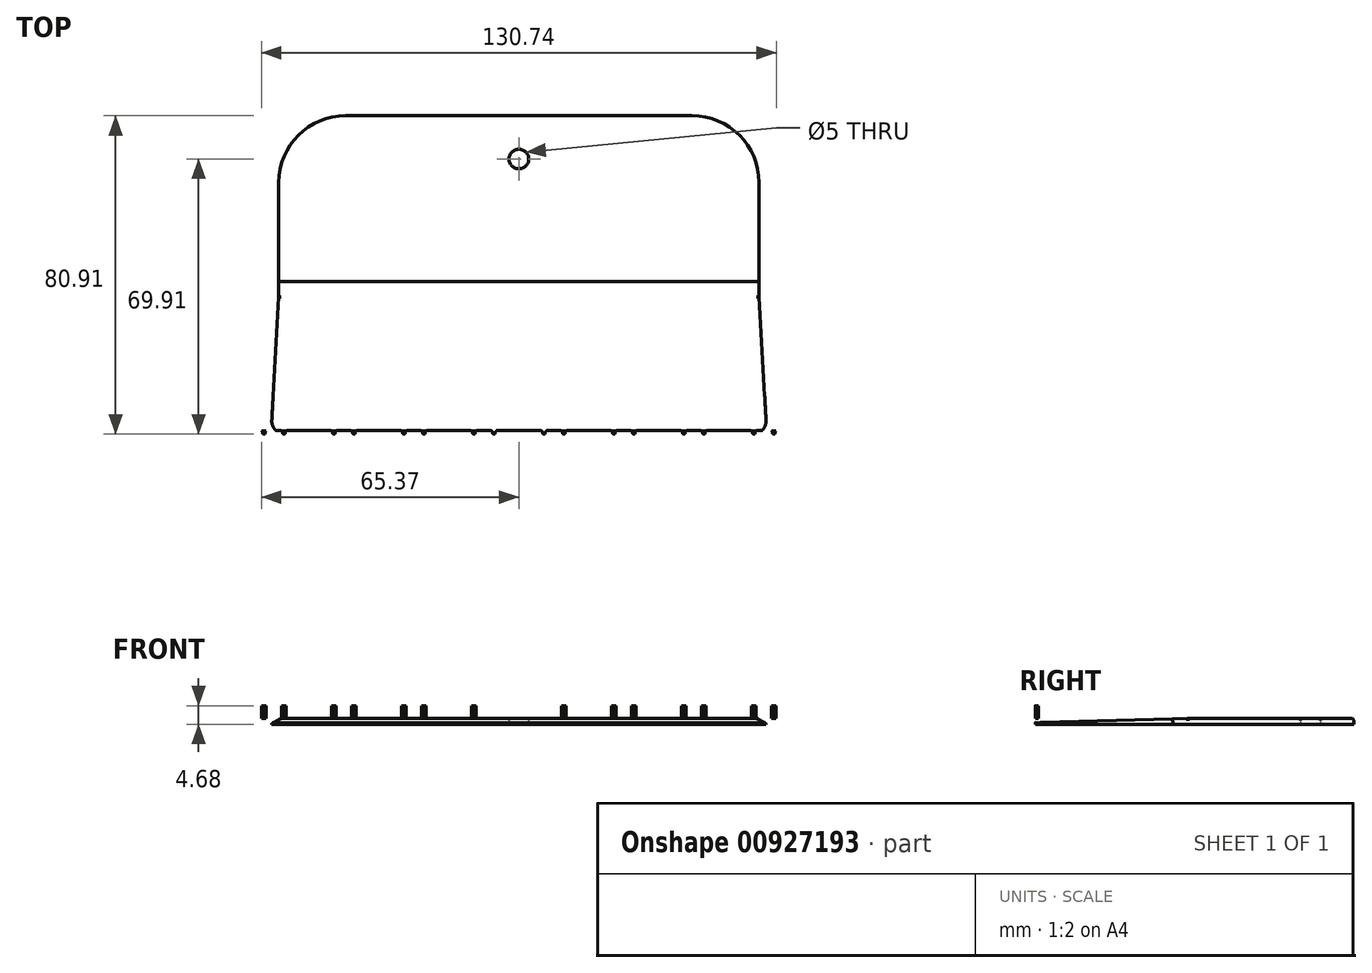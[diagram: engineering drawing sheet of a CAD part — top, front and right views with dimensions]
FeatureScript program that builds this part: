
annotation { "Feature Type Name" : "Feature", "Feature Type Description" : "" }
export const myFeature = defineFeature(function(context is Context, id is Id, definition is map)
    precondition{}
    {
        {
            var Q0;
            Q0=qCreatedBy(makeId("Top.planeOp"),FACE);
            var sketch = newSketch(context, id + "F0", { "sketchPlane" : qUnion([Q0])});
            skLineSegment(sketch, "E0.top", {"start": v(44, 40.5) * mm, "end": v(-44, 40.5) * mm});
            skPoint(sketch, "E1.orphan", {"position": v(61, 42) * mm});
            skPoint(sketch, "E2.orphan", {"position": v(-61, 42) * mm});
            skLineSegment(sketch, "E3", {"start": v(-74.02, -5.5) * mm, "end": v(79.96, -5.5) * mm, "construction": true});
            skPoint(sketch, "E4.orphan", {"position": v(-63, 40.5) * mm});
            skPoint(sketch, "E5.orphan", {"position": v(63, 40.5) * mm});
            skLineSegment(sketch, "E6.trimOffspring", {"start": v(-61, -5.5) * mm, "end": v(-61, 23.5) * mm});
            skLineSegment(sketch, "E7.trimOffspring", {"start": v(61, -5.5) * mm, "end": v(61, 23.5) * mm});
            skLineSegment(sketch, "E8", {"start": v(-61, -5.5) * mm, "end": v(-62.79, -36.8) * mm});
            skLineSegment(sketch, "E9", {"start": v(61, -5.5) * mm, "end": v(62.79, -36.8) * mm});
            skArc(sketch, "E10.filletArc", {"start": v(59.3, -40.5) * mm, "mid": v(61.84, -39.4) * mm, "end": v(62.79, -36.8) * mm});
            skArc(sketch, "E11.filletArc", {"start": v(-62.79, -36.8) * mm, "mid": v(-61.84, -39.4) * mm, "end": v(-59.3, -40.5) * mm});
            skPoint(sketch, "E12.visualSharp", {"position": v(-61, 40.5) * mm});
            skArc(sketch, "E12.filletArc", {"start": v(-44, 40.5) * mm, "mid": v(-56.02, 35.52) * mm, "end": v(-61, 23.5) * mm});
            skPoint(sketch, "E13.visualSharp", {"position": v(61, 40.5) * mm});
            skArc(sketch, "E13.filletArc", {"start": v(61, 23.5) * mm, "mid": v(56.02, 35.52) * mm, "end": v(44, 40.5) * mm});
            skCircle(sketch, "E14", {"center": v(0, 29.5) * mm, "radius": 2.5 * mm});
            skLineSegment(sketch, "E15", {"start": v(-59.3, -40.5) * mm, "end": v(59.3, -40.5) * mm});
            skPoint(sketch, "E15.endSnap0", {"position": v(59.3, -40.5) * mm});
            skSolve(sketch);
        }
        {
            var Q0;
            Q0 = qSketchRegion(id + "F0", true);
            extrude(context, id + "F1", {"entities" : qUnion([Q0]), "depth" : 1.5 * mm, "offsetDistance" : 25 * mm});
        }
        {
            var Q0;
            Q0=makeQuery(id+"F1.opExtrude","CAP_FACE",FACE,{"disambiguationData":[OSD([sQuery(id+"F0.wireOp",EDGE,"E0.top"),sQuery(id+"F0.wireOp",EDGE,"E6.trimOffspring"),sQuery(id+"F0.wireOp",EDGE,"E7.trimOffspring"),sQuery(id+"F0.wireOp",EDGE,"E8"),sQuery(id+"F0.wireOp",EDGE,"E9"),sQuery(id+"F0.wireOp",EDGE,"E10.filletArc"),sQuery(id+"F0.wireOp",EDGE,"E11.filletArc"),sQuery(id+"F0.wireOp",EDGE,"E12.filletArc"),sQuery(id+"F0.wireOp",EDGE,"E13.filletArc"),sQuery(id+"F0.wireOp",EDGE,"E14"),sQuery(id+"F0.wireOp",EDGE,"E15")])],"isStart":false});
            var sketch = newSketch(context, id + "F2", { "sketchPlane" : qUnion([Q0])});
            skLineSegment(sketch, "E16.3.0.1", {"start": v(-45.36, -39.59) * mm, "end": v(-56.24, -39.59) * mm});
            skPoint(sketch, "E16.4.0.0", {"position": v(-57.15, -39.97) * mm});
            skArc(sketch, "E16.4.0.3", {"start": v(-57.45, -40.2) * mm, "mid": v(-57.15, -40.5) * mm, "end": v(-56.85, -40.2) * mm});
            skLineSegment(sketch, "E16.4.0.5", {"start": v(-57.15, -39.2) * mm, "end": v(-57.15, -39.9) * mm, "construction": true});
            skArc(sketch, "E17.filletArc", {"start": v(-56.24, -39.59) * mm, "mid": v(-56.67, -39.76) * mm, "end": v(-56.85, -40.2) * mm});
            skPoint(sketch, "E18.visualSharp", {"position": v(-57.45, -39.2) * mm});
            skArc(sketch, "E19.MirrorCS", {"start": v(-58.06, -39.59) * mm, "mid": v(-57.63, -39.76) * mm, "end": v(-57.45, -40.2) * mm});
            skLineSegment(sketch, "E20.MirrorCS", {"start": v(-69.35, -39.59) * mm, "end": v(-58.06, -39.59) * mm});
            skArc(sketch, "E21.1.0.0", {"start": v(-45.36, -39.59) * mm, "mid": v(-44.93, -39.76) * mm, "end": v(-44.75, -40.2) * mm});
            skArc(sketch, "E21.1.0.1", {"start": v(-44.75, -40.2) * mm, "mid": v(-44.45, -40.5) * mm, "end": v(-44.15, -40.2) * mm});
            skArc(sketch, "E21.1.0.2", {"start": v(-43.54, -39.59) * mm, "mid": v(-43.97, -39.76) * mm, "end": v(-44.15, -40.2) * mm});
            skLineSegment(sketch, "E21.1.0.3", {"start": v(-32.66, -39.59) * mm, "end": v(-43.54, -39.59) * mm});
            skArc(sketch, "E21.2.0.0", {"start": v(-32.66, -39.59) * mm, "mid": v(-32.23, -39.76) * mm, "end": v(-32.05, -40.2) * mm});
            skArc(sketch, "E21.2.0.1", {"start": v(-32.05, -40.2) * mm, "mid": v(-31.75, -40.5) * mm, "end": v(-31.45, -40.2) * mm});
            skArc(sketch, "E21.2.0.2", {"start": v(-30.84, -39.59) * mm, "mid": v(-31.27, -39.76) * mm, "end": v(-31.45, -40.2) * mm});
            skLineSegment(sketch, "E21.2.0.3", {"start": v(-19.96, -39.59) * mm, "end": v(-30.84, -39.59) * mm});
            skArc(sketch, "E21.3.0.0", {"start": v(-19.96, -39.59) * mm, "mid": v(-19.53, -39.76) * mm, "end": v(-19.35, -40.2) * mm});
            skArc(sketch, "E21.3.0.1", {"start": v(-19.35, -40.2) * mm, "mid": v(-19.05, -40.5) * mm, "end": v(-18.75, -40.2) * mm});
            skArc(sketch, "E21.3.0.2", {"start": v(-18.14, -39.59) * mm, "mid": v(-18.57, -39.76) * mm, "end": v(-18.75, -40.2) * mm});
            skLineSegment(sketch, "E21.3.0.3", {"start": v(-6.85, -39.59) * mm, "end": v(-18.14, -39.59) * mm});
            skArc(sketch, "E21.4.0.0", {"start": v(-7.26, -39.59) * mm, "mid": v(-6.83, -39.76) * mm, "end": v(-6.65, -40.2) * mm});
            skArc(sketch, "E21.4.0.1", {"start": v(-6.65, -40.2) * mm, "mid": v(-6.35, -40.5) * mm, "end": v(-6.05, -40.2) * mm});
            skArc(sketch, "E21.4.0.2", {"start": v(-5.44, -39.59) * mm, "mid": v(-5.87, -39.76) * mm, "end": v(-6.05, -40.2) * mm});
            skLineSegment(sketch, "E21.4.0.3", {"start": v(5.85, -39.59) * mm, "end": v(-5.44, -39.59) * mm});
            skArc(sketch, "E21.5.0.0", {"start": v(5.44, -39.59) * mm, "mid": v(5.87, -39.76) * mm, "end": v(6.05, -40.2) * mm});
            skArc(sketch, "E21.5.0.1", {"start": v(6.05, -40.2) * mm, "mid": v(6.35, -40.5) * mm, "end": v(6.65, -40.2) * mm});
            skArc(sketch, "E21.5.0.2", {"start": v(7.26, -39.59) * mm, "mid": v(6.83, -39.76) * mm, "end": v(6.65, -40.2) * mm});
            skLineSegment(sketch, "E21.5.0.3", {"start": v(18.55, -39.59) * mm, "end": v(7.26, -39.59) * mm});
            skArc(sketch, "E21.6.0.0", {"start": v(18.14, -39.59) * mm, "mid": v(18.57, -39.76) * mm, "end": v(18.75, -40.2) * mm});
            skArc(sketch, "E21.6.0.1", {"start": v(18.75, -40.2) * mm, "mid": v(19.05, -40.5) * mm, "end": v(19.35, -40.2) * mm});
            skArc(sketch, "E21.6.0.2", {"start": v(19.96, -39.59) * mm, "mid": v(19.53, -39.76) * mm, "end": v(19.35, -40.2) * mm});
            skLineSegment(sketch, "E21.6.0.3", {"start": v(31.25, -39.59) * mm, "end": v(19.96, -39.59) * mm});
            skArc(sketch, "E21.7.0.0", {"start": v(30.84, -39.59) * mm, "mid": v(31.27, -39.76) * mm, "end": v(31.45, -40.2) * mm});
            skArc(sketch, "E21.7.0.1", {"start": v(31.45, -40.2) * mm, "mid": v(31.75, -40.5) * mm, "end": v(32.05, -40.2) * mm});
            skArc(sketch, "E21.7.0.2", {"start": v(32.66, -39.59) * mm, "mid": v(32.23, -39.76) * mm, "end": v(32.05, -40.2) * mm});
            skLineSegment(sketch, "E21.7.0.3", {"start": v(43.95, -39.59) * mm, "end": v(32.66, -39.59) * mm});
            skArc(sketch, "E21.8.0.0", {"start": v(43.54, -39.59) * mm, "mid": v(43.97, -39.76) * mm, "end": v(44.15, -40.2) * mm});
            skArc(sketch, "E21.8.0.1", {"start": v(44.15, -40.2) * mm, "mid": v(44.45, -40.5) * mm, "end": v(44.75, -40.2) * mm});
            skArc(sketch, "E21.8.0.2", {"start": v(45.36, -39.59) * mm, "mid": v(44.93, -39.76) * mm, "end": v(44.75, -40.2) * mm});
            skLineSegment(sketch, "E21.8.0.3", {"start": v(56.65, -39.59) * mm, "end": v(45.36, -39.59) * mm});
            skArc(sketch, "E21.9.0.0", {"start": v(56.24, -39.59) * mm, "mid": v(56.67, -39.76) * mm, "end": v(56.85, -40.2) * mm});
            skArc(sketch, "E21.9.0.1", {"start": v(56.85, -40.2) * mm, "mid": v(57.15, -40.5) * mm, "end": v(57.45, -40.2) * mm});
            skArc(sketch, "E21.9.0.2", {"start": v(58.06, -39.59) * mm, "mid": v(57.63, -39.76) * mm, "end": v(57.45, -40.2) * mm});
            skLineSegment(sketch, "E21.9.0.3", {"start": v(69.35, -39.59) * mm, "end": v(58.06, -39.59) * mm});
            skLineSegment(sketch, "E21.direction1", {"start": v(-58.06, -40.2) * mm, "end": v(-45.36, -40.2) * mm, "construction": true});
            skPoint(sketch, "E22.orphan", {"position": v(-44.95, -39.59) * mm});
            skPoint(sketch, "E23.orphan", {"position": v(-32.25, -39.59) * mm});
            skPoint(sketch, "E24.orphan", {"position": v(-19.55, -39.59) * mm});
            skLineSegment(sketch, "E25", {"start": v(-69.35, -39.59) * mm, "end": v(-69.35, -63.5) * mm});
            skLineSegment(sketch, "E26", {"start": v(-69.35, -63.5) * mm, "end": v(69.35, -63.5) * mm});
            skLineSegment(sketch, "E27", {"start": v(69.35, -63.5) * mm, "end": v(69.35, -39.59) * mm});
            skSolve(sketch);
        }
        {
            var Q0;
            Q0=qCreatedBy(makeId("Right.planeOp"),FACE);
            var sketch = newSketch(context, id + "F3", { "sketchPlane" : qUnion([Q0])});
            skLineSegment(sketch, "E28", {"start": v(0, 1.55) * mm, "end": v(-43.24, 0.26) * mm});
            skLineSegment(sketch, "E29", {"start": v(-43.24, 0.26) * mm, "end": v(-43.4, 5.8) * mm});
            skLineSegment(sketch, "E30", {"start": v(-43.4, 5.8) * mm, "end": v(0, 5.8) * mm});
            skLineSegment(sketch, "E31", {"start": v(0, 5.8) * mm, "end": v(0, 1.55) * mm});
            skSolve(sketch);
        }
        {
            var Q0;
            Q0 = qSketchRegion(id + "F3", true);
            extrude(context, id + "F4", {"entities" : qUnion([Q0]), "operationType" : NewBodyOperationType.REMOVE, "endBound" : BoundingType.SYMMETRIC, "oppositeDirection" : true, "depth" : 152.4 * mm, "offsetDistance" : 25.4 * mm});
        }
        {
            var Q0;
            Q0=makeQuery(id+"F1.opExtrude","CAP_EDGE",EDGE,{"disambiguationData":[OSD([sQuery(id+"F0.wireOp",EDGE,"E0.top")])],"isStart":false});
            fillet(context, id + "F5", {"entities" : qUnion([Q0]), "radius" : 0.64 * mm, "tangentPropagation" : true, "allowEdgeOverflow" : false});
        }
        {
            var Q0;
            Q0=makeQuery(id+"F1.opExtrude","CAP_EDGE",EDGE,{"disambiguationData":[OSD([sQuery(id+"F0.wireOp",EDGE,"E14")])],"isStart":false});
            fillet(context, id + "F6", {"entities" : qUnion([Q0]), "radius" : 0.5 * mm, "tangentPropagation" : true, "allowEdgeOverflow" : false});
        }
        {
            var Q0;
            Q0 = qSketchRegion(id + "F2", true);
            extrude(context, id + "F7", {"entities" : qUnion([Q0]), "depth" : 3.17 * mm, "offsetDistance" : 25.4 * mm});
        }
        {
            var Q0;
            Q0=qCreatedBy(makeId("Top.planeOp"),FACE);
            var sketch = newSketch(context, id + "F8", { "sketchPlane" : qUnion([Q0])});
            skArc(sketch, "E32", {"start": v(6.05, -40.11) * mm, "mid": v(6.35, -40.41) * mm, "end": v(6.65, -40.11) * mm});
            skArc(sketch, "E33", {"start": v(6.05, -40.11) * mm, "mid": v(5.87, -39.68) * mm, "end": v(5.44, -39.5) * mm});
            skLineSegment(sketch, "E34", {"start": v(-5.44, -39.5) * mm, "end": v(5.44, -39.5) * mm});
            skArc(sketch, "E35", {"start": v(-5.44, -39.5) * mm, "mid": v(-5.87, -39.68) * mm, "end": v(-6.05, -40.11) * mm});
            skArc(sketch, "E36", {"start": v(-6.65, -40.11) * mm, "mid": v(-6.35, -40.41) * mm, "end": v(-6.05, -40.11) * mm});
            skArc(sketch, "E37", {"start": v(-6.65, -40.11) * mm, "mid": v(-6.83, -39.68) * mm, "end": v(-7.26, -39.5) * mm});
            skLineSegment(sketch, "E38", {"start": v(-8.89, -39.5) * mm, "end": v(-7.26, -39.5) * mm});
            skLineSegment(sketch, "E39", {"start": v(7.26, -39.5) * mm, "end": v(8.89, -39.5) * mm});
            skArc(sketch, "E40", {"start": v(7.26, -39.5) * mm, "mid": v(6.83, -39.68) * mm, "end": v(6.65, -40.11) * mm});
            skArc(sketch, "E41", {"start": v(23.83, -40.11) * mm, "mid": v(24.13, -40.41) * mm, "end": v(24.43, -40.11) * mm});
            skArc(sketch, "E42", {"start": v(23.83, -40.11) * mm, "mid": v(23.65, -39.68) * mm, "end": v(23.22, -39.5) * mm});
            skLineSegment(sketch, "E43", {"start": v(12.34, -39.5) * mm, "end": v(23.22, -39.5) * mm});
            skArc(sketch, "E44", {"start": v(12.34, -39.5) * mm, "mid": v(11.9, -39.68) * mm, "end": v(11.73, -40.11) * mm});
            skArc(sketch, "E45", {"start": v(11.13, -40.11) * mm, "mid": v(11.43, -40.41) * mm, "end": v(11.73, -40.11) * mm});
            skArc(sketch, "E46", {"start": v(11.13, -40.11) * mm, "mid": v(10.95, -39.68) * mm, "end": v(10.52, -39.5) * mm});
            skLineSegment(sketch, "E47", {"start": v(8.89, -39.5) * mm, "end": v(10.52, -39.5) * mm});
            skLineSegment(sketch, "E48", {"start": v(25.04, -39.5) * mm, "end": v(26.67, -39.5) * mm});
            skArc(sketch, "E49", {"start": v(25.04, -39.5) * mm, "mid": v(24.6, -39.68) * mm, "end": v(24.43, -40.11) * mm});
            skArc(sketch, "E50", {"start": v(41.61, -40.11) * mm, "mid": v(41.9, -40.41) * mm, "end": v(42.2, -40.11) * mm});
            skArc(sketch, "E51", {"start": v(41.61, -40.11) * mm, "mid": v(41.43, -39.68) * mm, "end": v(41, -39.5) * mm});
            skLineSegment(sketch, "E52", {"start": v(30.12, -39.5) * mm, "end": v(41, -39.5) * mm});
            skArc(sketch, "E53", {"start": v(30.12, -39.5) * mm, "mid": v(29.69, -39.68) * mm, "end": v(29.5, -40.11) * mm});
            skArc(sketch, "E54", {"start": v(28.91, -40.11) * mm, "mid": v(29.2, -40.41) * mm, "end": v(29.5, -40.11) * mm});
            skArc(sketch, "E55", {"start": v(28.91, -40.11) * mm, "mid": v(28.73, -39.68) * mm, "end": v(28.3, -39.5) * mm});
            skLineSegment(sketch, "E56", {"start": v(26.67, -39.5) * mm, "end": v(28.3, -39.5) * mm});
            skLineSegment(sketch, "E57", {"start": v(42.82, -39.5) * mm, "end": v(44.45, -39.5) * mm});
            skArc(sketch, "E58", {"start": v(42.82, -39.5) * mm, "mid": v(42.39, -39.68) * mm, "end": v(42.2, -40.11) * mm});
            skArc(sketch, "E59", {"start": v(59.4, -40.11) * mm, "mid": v(59.69, -40.41) * mm, "end": v(59.99, -40.11) * mm});
            skArc(sketch, "E60", {"start": v(59.4, -40.11) * mm, "mid": v(59.21, -39.68) * mm, "end": v(58.78, -39.5) * mm});
            skLineSegment(sketch, "E61", {"start": v(47.9, -39.5) * mm, "end": v(58.78, -39.5) * mm});
            skArc(sketch, "E62", {"start": v(47.9, -39.5) * mm, "mid": v(47.47, -39.68) * mm, "end": v(47.29, -40.11) * mm});
            skArc(sketch, "E63", {"start": v(46.7, -40.11) * mm, "mid": v(46.99, -40.41) * mm, "end": v(47.29, -40.11) * mm});
            skArc(sketch, "E64", {"start": v(46.7, -40.11) * mm, "mid": v(46.51, -39.68) * mm, "end": v(46.08, -39.5) * mm});
            skLineSegment(sketch, "E65", {"start": v(44.45, -39.5) * mm, "end": v(46.08, -39.5) * mm});
            skLineSegment(sketch, "E66", {"start": v(60.6, -39.5) * mm, "end": v(62.23, -39.5) * mm});
            skArc(sketch, "E67", {"start": v(60.6, -39.5) * mm, "mid": v(60.17, -39.68) * mm, "end": v(59.99, -40.11) * mm});
            skArc(sketch, "E68", {"start": v(77.17, -40.11) * mm, "mid": v(77.47, -40.41) * mm, "end": v(77.77, -40.11) * mm});
            skArc(sketch, "E69", {"start": v(77.17, -40.11) * mm, "mid": v(77, -39.68) * mm, "end": v(76.56, -39.5) * mm});
            skLineSegment(sketch, "E70", {"start": v(65.68, -39.5) * mm, "end": v(76.56, -39.5) * mm});
            skArc(sketch, "E71", {"start": v(65.68, -39.5) * mm, "mid": v(65.25, -39.68) * mm, "end": v(65.07, -40.11) * mm});
            skArc(sketch, "E72", {"start": v(64.47, -40.11) * mm, "mid": v(64.77, -40.41) * mm, "end": v(65.07, -40.11) * mm});
            skArc(sketch, "E73", {"start": v(64.47, -40.11) * mm, "mid": v(64.3, -39.68) * mm, "end": v(63.86, -39.5) * mm});
            skLineSegment(sketch, "E74", {"start": v(62.23, -39.5) * mm, "end": v(63.86, -39.5) * mm});
            skLineSegment(sketch, "E75", {"start": v(78.38, -39.5) * mm, "end": v(80, -39.5) * mm});
            skArc(sketch, "E76", {"start": v(78.38, -39.5) * mm, "mid": v(77.95, -39.68) * mm, "end": v(77.77, -40.11) * mm});
            skArc(sketch, "E77", {"start": v(-11.73, -40.11) * mm, "mid": v(-11.43, -40.41) * mm, "end": v(-11.13, -40.11) * mm});
            skArc(sketch, "E78", {"start": v(-11.73, -40.11) * mm, "mid": v(-11.9, -39.68) * mm, "end": v(-12.34, -39.5) * mm});
            skLineSegment(sketch, "E79", {"start": v(-23.22, -39.5) * mm, "end": v(-12.34, -39.5) * mm});
            skArc(sketch, "E80", {"start": v(-23.22, -39.5) * mm, "mid": v(-23.65, -39.68) * mm, "end": v(-23.83, -40.11) * mm});
            skArc(sketch, "E81", {"start": v(-24.43, -40.11) * mm, "mid": v(-24.13, -40.41) * mm, "end": v(-23.83, -40.11) * mm});
            skArc(sketch, "E82", {"start": v(-24.43, -40.11) * mm, "mid": v(-24.6, -39.68) * mm, "end": v(-25.04, -39.5) * mm});
            skLineSegment(sketch, "E83", {"start": v(-26.67, -39.5) * mm, "end": v(-25.04, -39.5) * mm});
            skLineSegment(sketch, "E84", {"start": v(-10.52, -39.5) * mm, "end": v(-8.89, -39.5) * mm});
            skArc(sketch, "E85", {"start": v(-10.52, -39.5) * mm, "mid": v(-10.95, -39.68) * mm, "end": v(-11.13, -40.11) * mm});
            skArc(sketch, "E86", {"start": v(-29.5, -40.11) * mm, "mid": v(-29.2, -40.41) * mm, "end": v(-28.91, -40.11) * mm});
            skArc(sketch, "E87", {"start": v(-29.5, -40.11) * mm, "mid": v(-29.69, -39.68) * mm, "end": v(-30.12, -39.5) * mm});
            skLineSegment(sketch, "E88", {"start": v(-41, -39.5) * mm, "end": v(-30.12, -39.5) * mm});
            skArc(sketch, "E89", {"start": v(-41, -39.5) * mm, "mid": v(-41.43, -39.68) * mm, "end": v(-41.61, -40.11) * mm});
            skArc(sketch, "E90", {"start": v(-42.2, -40.11) * mm, "mid": v(-41.9, -40.41) * mm, "end": v(-41.61, -40.11) * mm});
            skArc(sketch, "E91", {"start": v(-42.2, -40.11) * mm, "mid": v(-42.39, -39.68) * mm, "end": v(-42.82, -39.5) * mm});
            skLineSegment(sketch, "E92", {"start": v(-44.45, -39.5) * mm, "end": v(-42.82, -39.5) * mm});
            skLineSegment(sketch, "E93", {"start": v(-28.3, -39.5) * mm, "end": v(-26.67, -39.5) * mm});
            skArc(sketch, "E94", {"start": v(-28.3, -39.5) * mm, "mid": v(-28.73, -39.68) * mm, "end": v(-28.91, -40.11) * mm});
            skArc(sketch, "E95", {"start": v(-47.29, -40.11) * mm, "mid": v(-46.99, -40.41) * mm, "end": v(-46.7, -40.11) * mm});
            skArc(sketch, "E96", {"start": v(-47.29, -40.11) * mm, "mid": v(-47.47, -39.68) * mm, "end": v(-47.9, -39.5) * mm});
            skLineSegment(sketch, "E97", {"start": v(-58.78, -39.5) * mm, "end": v(-47.9, -39.5) * mm});
            skArc(sketch, "E98", {"start": v(-58.78, -39.5) * mm, "mid": v(-59.21, -39.68) * mm, "end": v(-59.4, -40.11) * mm});
            skArc(sketch, "E99", {"start": v(-59.99, -40.11) * mm, "mid": v(-59.69, -40.41) * mm, "end": v(-59.4, -40.11) * mm});
            skArc(sketch, "E100", {"start": v(-59.99, -40.11) * mm, "mid": v(-60.17, -39.68) * mm, "end": v(-60.6, -39.5) * mm});
            skLineSegment(sketch, "E101", {"start": v(-62.23, -39.5) * mm, "end": v(-60.6, -39.5) * mm});
            skLineSegment(sketch, "E102", {"start": v(-46.08, -39.5) * mm, "end": v(-44.45, -39.5) * mm});
            skArc(sketch, "E103", {"start": v(-46.08, -39.5) * mm, "mid": v(-46.51, -39.68) * mm, "end": v(-46.7, -40.11) * mm});
            skArc(sketch, "E104", {"start": v(-65.07, -40.11) * mm, "mid": v(-64.77, -40.41) * mm, "end": v(-64.47, -40.11) * mm});
            skArc(sketch, "E105", {"start": v(-65.07, -40.11) * mm, "mid": v(-65.25, -39.68) * mm, "end": v(-65.68, -39.5) * mm});
            skLineSegment(sketch, "E106", {"start": v(-76.56, -39.5) * mm, "end": v(-65.68, -39.5) * mm});
            skArc(sketch, "E107", {"start": v(-76.56, -39.5) * mm, "mid": v(-77, -39.68) * mm, "end": v(-77.17, -40.11) * mm});
            skArc(sketch, "E108", {"start": v(-77.77, -40.11) * mm, "mid": v(-77.47, -40.41) * mm, "end": v(-77.17, -40.11) * mm});
            skArc(sketch, "E109", {"start": v(-77.77, -40.11) * mm, "mid": v(-77.95, -39.68) * mm, "end": v(-78.38, -39.5) * mm});
            skLineSegment(sketch, "E110", {"start": v(-80, -39.5) * mm, "end": v(-78.38, -39.5) * mm});
            skLineSegment(sketch, "E111", {"start": v(-63.86, -39.5) * mm, "end": v(-62.23, -39.5) * mm});
            skArc(sketch, "E112", {"start": v(-63.86, -39.5) * mm, "mid": v(-64.3, -39.68) * mm, "end": v(-64.47, -40.11) * mm});
            skLineSegment(sketch, "E113", {"start": v(-80, -39.5) * mm, "end": v(-80, -68.64) * mm});
            skLineSegment(sketch, "E114", {"start": v(-80, -68.64) * mm, "end": v(80, -68.64) * mm});
            skLineSegment(sketch, "E115", {"start": v(80, -68.64) * mm, "end": v(80, -39.5) * mm});
            skSolve(sketch);
        }
        {
            var Q0;
            Q0 = qSketchRegion(id + "F8", true);
            extrude(context, id + "F9", {"entities" : qUnion([Q0]), "operationType" : NewBodyOperationType.REMOVE, "depth" : 25.4 * mm, "offsetDistance" : 25.4 * mm});
        }
    });
